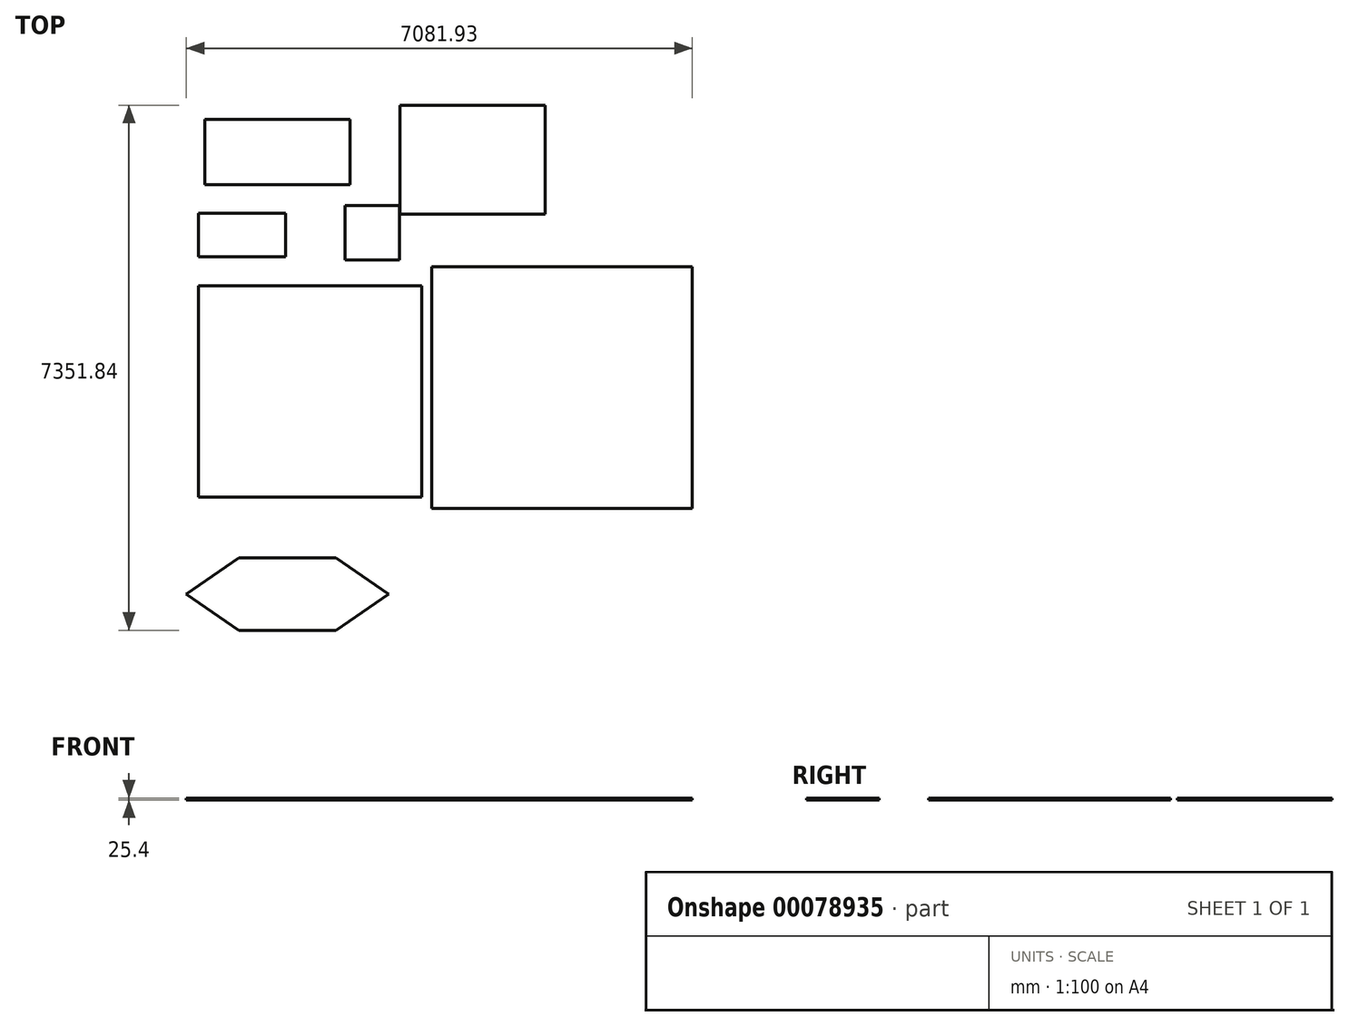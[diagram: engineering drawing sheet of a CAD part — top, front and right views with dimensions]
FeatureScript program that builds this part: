
annotation { "Feature Type Name" : "Feature", "Feature Type Description" : "" }
export const myFeature = defineFeature(function(context is Context, id is Id, definition is map)
    precondition{}
    {
        {
            var Q0;
            Q0=qCreatedBy(makeId("Top.planeOp"),FACE);
            var sketch = newSketch(context, id + "F0", { "sketchPlane" : qUnion([Q0])});
            skLineSegment(sketch, "E0.bottom", {"start": v(0, 0) * mm, "end": v(3124.2, 0) * mm});
            skLineSegment(sketch, "E0.top", {"start": v(0, 2959.1) * mm, "end": v(3124.2, 2959.1) * mm});
            skLineSegment(sketch, "E0.left", {"start": v(0, 0) * mm, "end": v(0, 2959.1) * mm});
            skLineSegment(sketch, "E0.right", {"start": v(3124.2, 0) * mm, "end": v(3124.2, 2959.1) * mm});
            skSolve(sketch);
        }
        {
            var Q0;
            Q0 = qSketchRegion(id + "F0", true);
            extrude(context, id + "F1", {"entities" : qUnion([Q0]), "depth" : 25.4 * mm});
        }
        {
            var Q0;
            Q0=qCreatedBy(makeId("Top.planeOp"),FACE);
            var sketch = newSketch(context, id + "F2", { "sketchPlane" : qUnion([Q0])});
            skLineSegment(sketch, "E1.bottom", {"start": v(3268.18, -160.82) * mm, "end": v(6913.08, -160.82) * mm});
            skLineSegment(sketch, "E1.top", {"start": v(3268.18, 3223.73) * mm, "end": v(6913.08, 3223.73) * mm});
            skLineSegment(sketch, "E1.left", {"start": v(3268.18, -160.82) * mm, "end": v(3268.18, 3223.73) * mm});
            skLineSegment(sketch, "E1.right", {"start": v(6913.08, -160.82) * mm, "end": v(6913.08, 3223.73) * mm});
            skSolve(sketch);
        }
        {
            var Q0;
            Q0 = qSketchRegion(id + "F2", true);
            extrude(context, id + "F3", {"entities" : qUnion([Q0]), "depth" : 25.4 * mm});
        }
        {
            var Q0;
            Q0=qCreatedBy(makeId("Top.planeOp"),FACE);
            var sketch = newSketch(context, id + "F4", { "sketchPlane" : qUnion([Q0])});
            skLineSegment(sketch, "E2.bottom", {"start": v(567.75, -848.85) * mm, "end": v(1926.65, -848.85) * mm});
            skLineSegment(sketch, "E2.top", {"start": v(567.75, -1864.85) * mm, "end": v(1926.65, -1864.85) * mm});
            skLineSegment(sketch, "E2.left", {"start": v(567.75, -848.85) * mm, "end": v(567.75, -1864.85) * mm});
            skLineSegment(sketch, "E2.right", {"start": v(1926.65, -848.85) * mm, "end": v(1926.65, -1864.85) * mm});
            skLineSegment(sketch, "E3", {"start": v(1926.65, -848.85) * mm, "end": v(2663.25, -1356.85) * mm});
            skLineSegment(sketch, "E4", {"start": v(2663.25, -1356.85) * mm, "end": v(1926.65, -1864.85) * mm});
            skLineSegment(sketch, "E5", {"start": v(567.75, -848.85) * mm, "end": v(-168.85, -1356.85) * mm});
            skLineSegment(sketch, "E6", {"start": v(-168.85, -1356.85) * mm, "end": v(567.75, -1864.85) * mm});
            skSolve(sketch);
        }
        {
            var Q0;
            Q0 = qSketchRegion(id + "F4", true);
            extrude(context, id + "F5", {"entities" : qUnion([Q0]), "depth" : 25.4 * mm});
        }
        {
            var Q0;
            Q0=qCreatedBy(makeId("Top.planeOp"),FACE);
            var sketch = newSketch(context, id + "F6", { "sketchPlane" : qUnion([Q0])});
            skLineSegment(sketch, "E7.bottom", {"start": v(0, 3365.98) * mm, "end": v(1219.2, 3365.98) * mm});
            skLineSegment(sketch, "E7.top", {"start": v(0, 3975.58) * mm, "end": v(1219.2, 3975.58) * mm});
            skLineSegment(sketch, "E7.left", {"start": v(0, 3365.98) * mm, "end": v(0, 3975.58) * mm});
            skLineSegment(sketch, "E7.right", {"start": v(1219.2, 3365.98) * mm, "end": v(1219.2, 3975.58) * mm});
            skSolve(sketch);
        }
        {
            var Q0;
            Q0 = qSketchRegion(id + "F6", true);
            extrude(context, id + "F7", {"entities" : qUnion([Q0]), "depth" : 25.4 * mm});
        }
        {
            var Q0;
            Q0=qCreatedBy(makeId("Top.planeOp"),FACE);
            var sketch = newSketch(context, id + "F8", { "sketchPlane" : qUnion([Q0])});
            skLineSegment(sketch, "E8.bottom", {"start": v(91.52, 4376.76) * mm, "end": v(2123.52, 4376.76) * mm});
            skLineSegment(sketch, "E8.top", {"start": v(91.52, 5291.16) * mm, "end": v(2123.52, 5291.16) * mm});
            skLineSegment(sketch, "E8.left", {"start": v(91.52, 4376.76) * mm, "end": v(91.52, 5291.16) * mm});
            skLineSegment(sketch, "E8.right", {"start": v(2123.52, 4376.76) * mm, "end": v(2123.52, 5291.16) * mm});
            skSolve(sketch);
        }
        {
            var Q0;
            Q0 = qSketchRegion(id + "F8", true);
            extrude(context, id + "F9", {"entities" : qUnion([Q0]), "depth" : 25.4 * mm});
        }
        {
            var Q0;
            Q0=qCreatedBy(makeId("Top.planeOp"),FACE);
            var sketch = newSketch(context, id + "F10", { "sketchPlane" : qUnion([Q0])});
            skLineSegment(sketch, "E9.bottom", {"start": v(2054.48, 4080.7) * mm, "end": v(2816.48, 4080.7) * mm});
            skLineSegment(sketch, "E9.top", {"start": v(2054.48, 3318.7) * mm, "end": v(2816.48, 3318.7) * mm});
            skLineSegment(sketch, "E9.left", {"start": v(2054.48, 4080.7) * mm, "end": v(2054.48, 3318.7) * mm});
            skLineSegment(sketch, "E9.right", {"start": v(2816.48, 4080.7) * mm, "end": v(2816.48, 3318.7) * mm});
            skSolve(sketch);
        }
        {
            var Q0;
            Q0 = qSketchRegion(id + "F10", true);
            extrude(context, id + "F11", {"entities" : qUnion([Q0]), "depth" : 25.4 * mm});
        }
        {
            var Q0;
            Q0=qCreatedBy(makeId("Top.planeOp"),FACE);
            var sketch = newSketch(context, id + "F12", { "sketchPlane" : qUnion([Q0])});
            skLineSegment(sketch, "E10.bottom", {"start": v(2823.77, 5487) * mm, "end": v(4855.77, 5487) * mm});
            skLineSegment(sketch, "E10.top", {"start": v(2823.77, 3963) * mm, "end": v(4855.77, 3963) * mm});
            skLineSegment(sketch, "E10.left", {"start": v(2823.77, 5487) * mm, "end": v(2823.77, 3963) * mm});
            skLineSegment(sketch, "E10.right", {"start": v(4855.77, 5487) * mm, "end": v(4855.77, 3963) * mm});
            skSolve(sketch);
        }
        {
            var Q0;
            Q0 = qSketchRegion(id + "F12", true);
            extrude(context, id + "F13", {"entities" : qUnion([Q0]), "depth" : 25.4 * mm});
        }
    });
